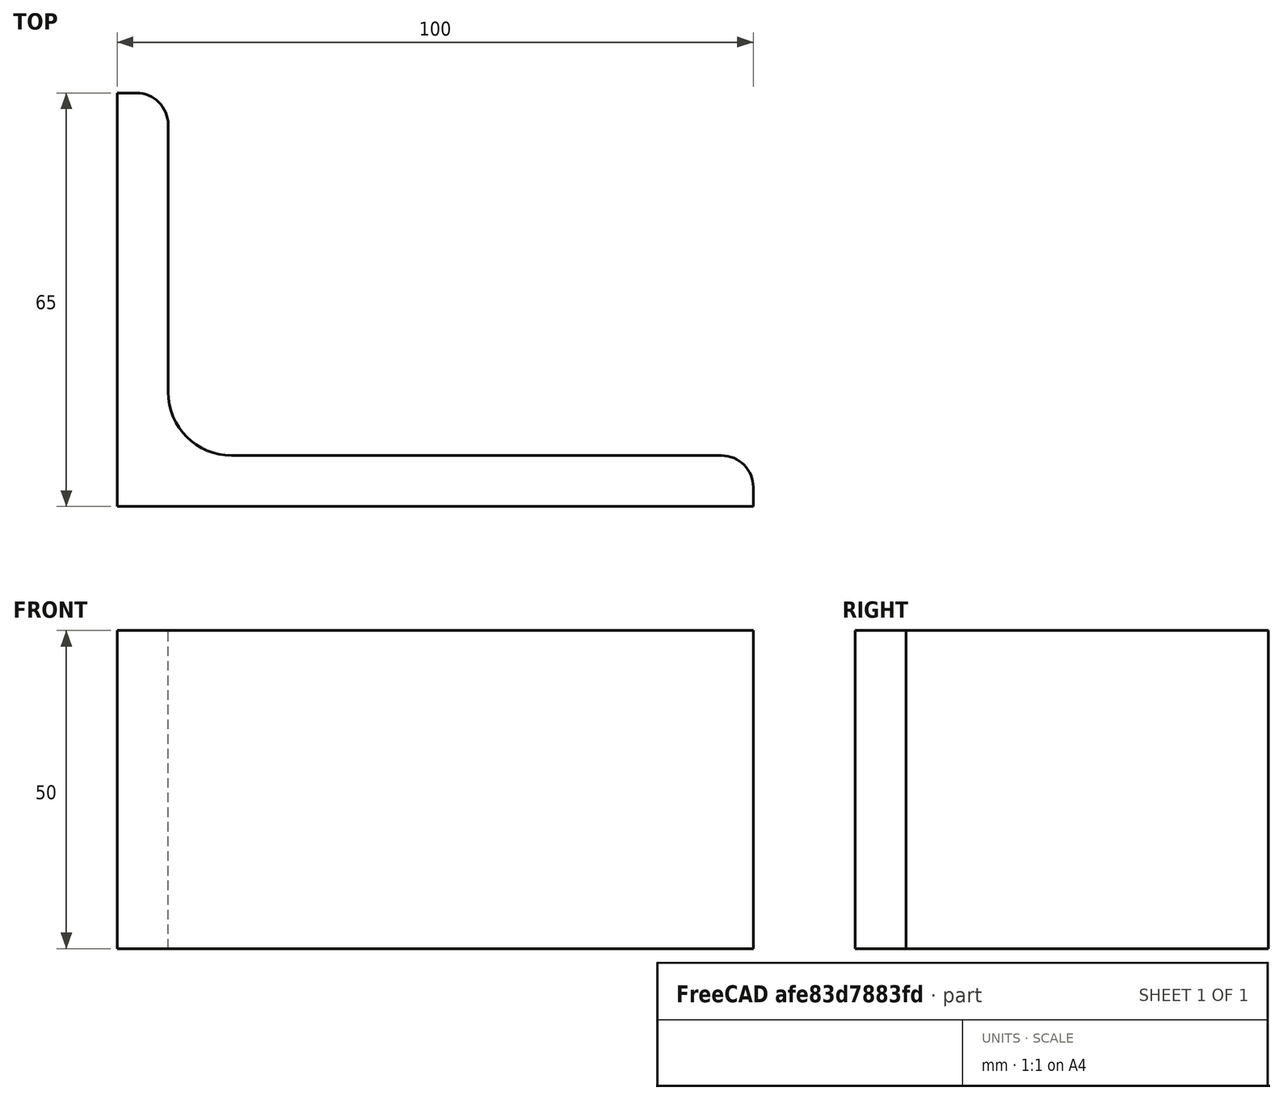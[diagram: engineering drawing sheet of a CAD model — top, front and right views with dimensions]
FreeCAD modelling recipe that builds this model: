
FCSTD DOCUMENT  (FreeCAD 0.15R4671 (Git))
Label: Angle Bar 100x65x8 EN10056 S235JR
License: All rights reserved
LicenseURL: http://en.wikipedia.org/wiki/All_rights_reserved
objects: Sketcher::SketchObject×1, Part::Extrusion×1
note: 2 computed .brp shape members not serialized (recipe doc carries the construction recipe); baked Part::Feature solids carry a one-line shape summary decoded from their .brp

FEATURE [Sketcher::SketchObject] Sketch
  sketch-geometry (9):
    g0: LineSegment StartX=0 StartY=0 StartZ=0 EndX=100 EndY=0 EndZ=0
    g1: LineSegment StartX=100 StartY=0 StartZ=0 EndX=100 EndY=3 EndZ=0
    g2: LineSegment StartX=95 StartY=8 StartZ=0 EndX=18 EndY=8 EndZ=0
    g3: LineSegment StartX=0 StartY=0 StartZ=0 EndX=0 EndY=65 EndZ=0
    g4: LineSegment StartX=0 StartY=65 StartZ=0 EndX=3 EndY=65 EndZ=0
    g5: LineSegment StartX=8 StartY=60 StartZ=0 EndX=8 EndY=18 EndZ=0
    g6: ArcOfCircle CenterX=18 CenterY=18 CenterZ=0 NormalX=0 NormalY=0 NormalZ=1 Radius=10 StartAngle=3.14159 EndAngle=4.71239
    g7: ArcOfCircle CenterX=3 CenterY=60 CenterZ=0 NormalX=0 NormalY=0 NormalZ=1 Radius=5 StartAngle=0 EndAngle=1.5708
    g8: ArcOfCircle CenterX=95 CenterY=3 CenterZ=0 NormalX=0 NormalY=0 NormalZ=1 Radius=5 StartAngle=0 EndAngle=1.5708
  constraints (23):
    c: Coincident(g0,g-1)
    c: Horizontal(g0)
    c: Coincident(g1,g0)
    c: Vertical(g1)
    c: Horizontal(g2)
    c: Coincident(g3,g-1)
    c: Vertical(g3)
    c: Coincident(g4,g3)
    c: Horizontal(g4)
    c: Vertical(g5)
    c: Tangent(g5,g6) = -1.5708
    c: Tangent(g2,g6) = 1.5708
    c: Tangent(g4,g7) = 1.5708
    c: Tangent(g5,g7) = 1.5708
    c: Tangent(g2,g8) = -1.5708
    c: Tangent(g1,g8) = -1.5708
    c: DistanceX(g0) = 100
    c: DistanceY(g3) = 65
    c: DistanceY(g0,g2) = 8
    c: DistanceX(g3,g5) = 8
    c: Radius(g6) = 10
    c: Radius(g8) = 5
    c: Radius(g7) = 5
FEATURE [Part::Extrusion] Extrude  label="Angle Bar 100x65x8 EN10056 S235JR"
  Base = -> Sketch
  Dir = (0,0,50)
  Solid = true
